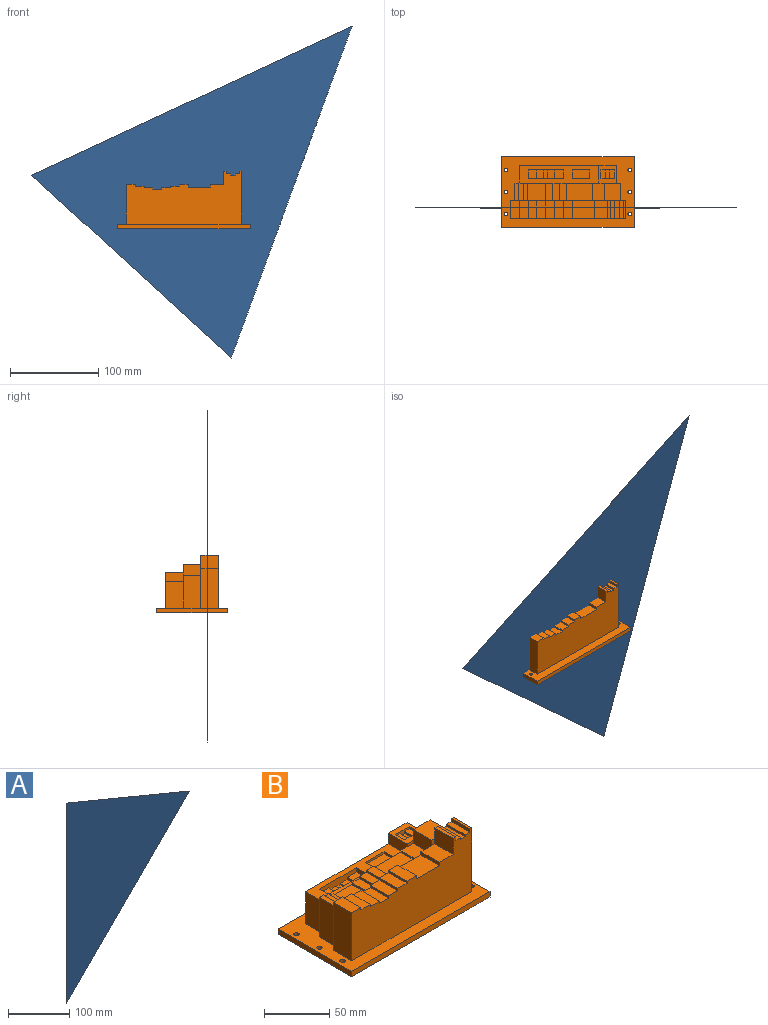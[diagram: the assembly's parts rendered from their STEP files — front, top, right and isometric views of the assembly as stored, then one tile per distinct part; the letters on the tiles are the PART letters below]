
ASSEMBLY  parts=2 mates=1
PART A: 5 faces, bbox 282.8x0.1x400 mm
  f0: plane 400x0.1mm, normal (-1,0,0), area 40mm2, adj f1,f2,f3,f4
  f1: plane 282.84x282.84mm, normal (0.71,0,-0.71), area 40mm2, adj f0,f2,f3,f4
  f2: plane 282.84x117.16mm, normal (0.38,0,0.92), area 30.6mm2, adj f0,f1,f3,f4
  f3: plane 400x282.84mm, normal (0,-1,0), area 56568.5mm2, adj f0,f1,f2
  f4: plane 400x282.84mm, normal (0,1,0), area 56568.5mm2, adj f0,f1,f2
PART B: 102 faces, bbox 150x80x65 mm
  f0: plane 50x18.43mm, normal (0,1,0), area 384.2mm2, adj f9,f14,f26,f28,f29,f83
  f1: plane 95x37.18mm, normal (0,1,0), area 598.6mm2, adj f2,f12,f13,f14,f33,f84,f85,f86
  f2: plane 37.18x20mm, normal (-1,0,0), area 743.6mm2, adj f1,f7,f14,f100
  f3: plane 5x3.43mm, normal (0,-1,0), area 17.1mm2, adj f29,f81,f82,f83
  f4: plane 20x3mm, normal (0,0,1), area 60mm2, adj f6,f32,f58,f82
  f5: plane 20x2mm, normal (0,0,1), area 40mm2, adj f6,f30,f32,f64
  f6: plane 60x20mm, normal (0,1,0), area 395mm2, adj f4,f5,f14,f28,f29,f30,f58,f59
  f7: plane 106.58x45mm, normal (0,1,0), area 997.9mm2, adj f2,f14,f31,f65,f66,f67,f68,f69
  f8: plane 10x5mm, normal (0,0,1), area 50mm2, adj f51,f52,f53,f56
  f9: plane 20x20mm, normal (0,0,1), area 250mm2, adj f0,f26,f27,f33,f50,f51,f52,f53
  f10: plane 10x7.5mm, normal (0,0,1), area 75mm2, adj f39,f41,f45,f48
  f11: plane 10x10mm, normal (0,0,1), area 100mm2, adj f39,f40,f41,f44
  f12: plane 90x20mm, normal (0,0,1), area 1200mm2, adj f1,f13,f27,f33,f34,f35,f36,f37
  f13: plane 30x20mm, normal (-1,0,0), area 600mm2, adj f1,f12,f14,f27
  f14: plane 150x80mm, normal (0,0,1), area 4724.6mm2, adj f0,f1,f2,f6,f7,f13,f15,f16
  f15: plane 80x5mm, normal (1,0,0), area 400mm2, adj f14,f16,f23,f25
  f16: plane 150x5mm, normal (0,1,0), area 750mm2, adj f14,f15,f17,f25
  f17: plane 80x5mm, normal (-1,0,0), area 400mm2, adj f14,f16,f23,f25
  f18: cylinder r=2mm len=5mm, axis (0,0,-1), area 62.8mm2, adj f14,f25
  f19: cylinder r=2mm len=5mm, axis (0,0,-1), area 62.8mm2, adj f14,f25
  f20: cylinder r=2mm len=5mm, axis (0,0,-1), area 62.8mm2, adj f14,f25
  f21: cylinder r=2mm len=5mm, axis (0,0,-1), area 62.8mm2, adj f14,f25
  f22: cylinder r=2mm len=5mm, axis (0,0,-1), area 62.8mm2, adj f14,f25
  f23: plane 150x5mm, normal (0,-1,0), area 750mm2, adj f14,f15,f17,f25
  f24: cylinder r=2mm len=5mm, axis (0,0,-1), area 62.8mm2, adj f14,f25
  f25: plane 150x80mm, normal (0,0,-1), area 11924.6mm2, adj f15,f16,f17,f18,f19,f20,f21,f22
  f26: plane 40x20mm, normal (1,0,0), area 800mm2, adj f0,f9,f14,f27
  f27: plane 110x40mm, normal (0,1,0), area 3500mm2, adj f9,f12,f13,f14,f26,f33
  f28: plane 50x20mm, normal (1,0,0), area 1000mm2, adj f0,f6,f14,f29
  f29: plane 20x18.43mm, normal (0,0,1), area 368.5mm2, adj f0,f3,f6,f28,f83
  f30: plane 60x20mm, normal (1,0,0), area 1200mm2, adj f5,f6,f14,f32
  f31: plane 45x20mm, normal (-1,0,0), area 900mm2, adj f7,f14,f32,f65
  f32: plane 130x60mm, normal (0,-1,0), area 5840mm2, adj f4,f5,f14,f30,f31,f58,f59,f60
  f33: plane 20x10mm, normal (-1,0,0), area 200mm2, adj f1,f9,f12,f27,f101
  f34: plane 20x2mm, normal (0,-1,0), area 40mm2, adj f12,f35,f37,f38
  f35: plane 10x2mm, normal (1,0,0), area 20mm2, adj f12,f34,f36,f38
  f36: plane 20x2mm, normal (0,1,0), area 40mm2, adj f12,f35,f37,f38
  f37: plane 10x2mm, normal (-1,0,0), area 20mm2, adj f12,f34,f36,f38
  f38: plane 20x10mm, normal (0,0,1), area 200mm2, adj f34,f35,f36,f37
  f39: plane 40x7mm, normal (0,1,0), area 205mm2, adj f10,f11,f12,f40,f42,f43,f44,f45
  f40: plane 10x4mm, normal (-1,0,0), area 40mm2, adj f11,f12,f39,f41
  f41: plane 40x7mm, normal (0,-1,0), area 205mm2, adj f10,f11,f12,f40,f42,f43,f44,f45
  f42: plane 10x4mm, normal (1,0,0), area 40mm2, adj f12,f39,f41,f43
  f43: plane 10x10mm, normal (0,0,1), area 100mm2, adj f39,f41,f42,f45
  f44: plane 10x2mm, normal (-1,0,0), area 20mm2, adj f11,f39,f41,f46
  f45: plane 10x2mm, normal (1,0,0), area 20mm2, adj f10,f39,f41,f43
  f46: plane 10x7.5mm, normal (0,0,1), area 75mm2, adj f39,f41,f44,f47
  f47: plane 10x1mm, normal (-1,0,0), area 10mm2, adj f39,f41,f46,f49
  f48: plane 10x1mm, normal (1,0,0), area 10mm2, adj f10,f39,f41,f49
  f49: plane 10x5mm, normal (0,0,1), area 50mm2, adj f39,f41,f47,f48
  f50: plane 10x2mm, normal (-1,0,0), area 20mm2, adj f9,f51,f53,f54
  f51: plane 15x4mm, normal (0,-1,0), area 40mm2, adj f8,f9,f50,f52,f54,f55,f56,f57
  f52: plane 10x2mm, normal (1,0,0), area 20mm2, adj f8,f9,f51,f53
  f53: plane 15x4mm, normal (0,1,0), area 40mm2, adj f8,f9,f50,f52,f54,f55,f56,f57
  f54: plane 10x5mm, normal (0,0,1), area 50mm2, adj f50,f51,f53,f55
  f55: plane 10x2mm, normal (-1,0,0), area 20mm2, adj f51,f53,f54,f57
  f56: plane 10x2mm, normal (1,0,0), area 20mm2, adj f8,f51,f53,f57
  f57: plane 10x5mm, normal (0,0,1), area 50mm2, adj f51,f53,f55,f56
  f58: plane 20x3mm, normal (1,0,0), area 60mm2, adj f4,f6,f32,f59
  f59: plane 20x5mm, normal (0,0,1), area 100mm2, adj f6,f32,f58,f60
  f60: plane 20x2mm, normal (1,0,0), area 40mm2, adj f6,f32,f59,f61
  f61: plane 20x5mm, normal (0,0,1), area 100mm2, adj f6,f32,f60,f62
  f62: plane 20x2mm, normal (-1,0,0), area 40mm2, adj f6,f32,f61,f63
  f63: plane 20x5mm, normal (0,0,1), area 100mm2, adj f6,f32,f62,f64
  f64: plane 20x3mm, normal (-1,0,0), area 60mm2, adj f5,f6,f32,f63
  f65: plane 20x10mm, normal (0,0,1), area 200mm2, adj f7,f31,f32,f66
  f66: plane 20x2mm, normal (1,0,0), area 40mm2, adj f7,f32,f65,f67
  f67: plane 20x10mm, normal (0,0,1), area 200mm2, adj f7,f32,f66,f68
  f68: plane 20x2mm, normal (1,0,0), area 40mm2, adj f7,f32,f67,f69
  f69: plane 20x10mm, normal (0,0,1), area 200mm2, adj f7,f32,f68,f70
  f70: plane 20x2mm, normal (1,0,0), area 40mm2, adj f7,f32,f69,f71
  f71: plane 20x10mm, normal (0,0,1), area 200mm2, adj f7,f32,f70,f72
  f72: plane 20x2mm, normal (-1,0,0), area 40mm2, adj f7,f32,f71,f73
  f73: plane 20x10mm, normal (0,0,1), area 200mm2, adj f7,f32,f72,f74
  f74: plane 20x2mm, normal (-1,0,0), area 40mm2, adj f7,f32,f73,f75
  f75: plane 20x10mm, normal (0,0,1), area 200mm2, adj f7,f32,f74,f76
  f76: plane 20x2mm, normal (-1,0,0), area 40mm2, adj f7,f32,f75,f77
  f77: plane 20x10mm, normal (0,0,1), area 200mm2, adj f7,f32,f76,f78
  f78: plane 20x3mm, normal (1,0,0), area 60mm2, adj f7,f32,f77,f79
  f79: plane 25x20mm, normal (0,0,1), area 500mm2, adj f7,f32,f78,f80
  f80: plane 20x3mm, normal (-1,0,0), area 60mm2, adj f7,f32,f79,f81
  f81: plane 20x15mm, normal (0,0,1), area 300mm2, adj f3,f7,f32,f80,f82
  f82: plane 20x15mm, normal (-1,0,0), area 300mm2, adj f3,f4,f6,f32,f81
  f83: plane 20x12.82mm, normal (-1,0,0), area 256.4mm2, adj f0,f3,f7,f29,f84,f101
  f84: plane 20x13.42mm, normal (0,0,1), area 268.3mm2, adj f1,f7,f83,f85,f101
  f85: plane 20x1.62mm, normal (-1,0,0), area 32.4mm2, adj f1,f7,f84,f86
  f86: plane 29.67x20mm, normal (0,0,1), area 593.3mm2, adj f1,f7,f85,f87
  f87: plane 20x1.62mm, normal (1,0,0), area 32.4mm2, adj f1,f7,f86,f88
  f88: plane 20x7.71mm, normal (0,0,1), area 154.1mm2, adj f1,f7,f87,f89
  f89: plane 20x1.78mm, normal (-1,0,0), area 35.7mm2, adj f1,f7,f88,f90
  f90: plane 20x7.7mm, normal (0,0,1), area 153.9mm2, adj f1,f7,f89,f91
  f91: plane 20x2.11mm, normal (-1,0,0), area 42.1mm2, adj f1,f7,f90,f92
  f92: plane 20x7.94mm, normal (0,0,1), area 158.9mm2, adj f1,f7,f91,f93
  f93: plane 20x1.62mm, normal (-1,0,0), area 32.4mm2, adj f1,f7,f92,f94
  f94: plane 20.43x20mm, normal (0,0,1), area 408.5mm2, adj f1,f7,f93,f95
  f95: plane 20x1.62mm, normal (1,0,0), area 32.4mm2, adj f1,f7,f94,f96
  f96: plane 20x4.7mm, normal (0,0,1), area 94mm2, adj f1,f7,f95,f97
  f97: plane 20x2.11mm, normal (1,0,0), area 42.1mm2, adj f1,f7,f96,f98
  f98: plane 20x5.51mm, normal (0,0,1), area 110.2mm2, adj f1,f7,f97,f99
  f99: plane 20x1.78mm, normal (1,0,0), area 35.7mm2, adj f1,f7,f98,f100
  f100: plane 20x4.51mm, normal (0,0,1), area 90.2mm2, adj f1,f2,f7,f99
  f101: plane 6.58x2.82mm, normal (0,-1,0), area 18.6mm2, adj f9,f33,f83,f84
PLACE A rot(axis=(0,-1,0),160deg) t=(190.46,-18,229.4)mm
PLACE B at identity
MATE parallel A.f4 <-> B.f27  axis (0,1,0) through (24.02,-18,47.76)mm
